# Revit family: Furniture-Table-Casual-Naughtone-Trace_Circular_Table_Small
name_source: partatom
category: Furniture
revit_build: Autodesk Revit 2014 (Build: 20130308_1515(x64)
units: mm (PartAtom-declared; Revit-internal decimal feet)

## types (2) — shared parameters
COBie Description = Designed by InTheDetail, The trace table range is simply a modern classic that speaks for itself. Suffice to say, the immaculate hand made steel frame and repetition of shapes make trace an exquisitely balanced form.
Current Revision = 1
Height = 350 mm  [stored 1.14829 ft]
Manufacturer = Naughtone
Material Table = Laminate-White-Smooth
Name = Furniture-Table-Casual-Naughtone-Trace
Product URL = http://www.naughtone.com
Type Comments = Trace Table Small
URL = http://www.naughtone.com
Uniclass = Pr_40_50_21_58
WarrantyDuration = 60
zero-valued in all types: Barcode, Cost, SerialNumber, TagNumber

## per-type parameters (varying)
| type | AssetIdentifier | Depth | Description | Length | Model | Product Code | TypeName |
| TRA-800-DIA | TR-800-DIA | 800 mm  [stored 2.62467 ft] | Trace Circular Table 800mm | 800 mm  [stored 2.62467 ft] | Trace Circular Table 800mm | TR-800-DIA | 800mmx800mmx350mm, Trace Table Small |
| TRA-600-DIA | TRA-600-DIA | 600 mm | Trace Circular Table 600mm | 600 mm | Trace Circular Table 600mm | TRA-600-DIA | 600mmx600mmx350mm, Trace Table Small |

note: [stored X ft] marks values corroborated as IEEE doubles in the binary element streams (Revit-internal decimal feet)

## geometry (parser evidence)
native form markers: Sweep x1
no freeform markers — native parametric forms only
